# Revit family: Sink-Vessel-Lavatory-KOHLER-Spacity-K-28907T
name_source: partatom
category: Plumbing Fixtures
units: mm (PartAtom-declared; Revit-internal decimal feet)

## family parameters
Cut with Voids When Loaded = No
Host = Face
OmniClass Number = 23.31.13.00
OmniClass Title = Sinks
Part Type = Normal
Room Calculation Point = No
Round Connector Dimension = Use Diameter
Shared = No

## types (1)
- 0-White
    ADA Compliant = No
    Assembly Code = D2010400
    CW Connection = No
    Cold Water Inlet = Cold Water Inlet
    Date Modified = 19/01/2023
    Default Elevation = 36"
    Description = SQUARE VESSEL WITH DECK
    Drain Included = No
    Finish = Kohler-Vitreous_China-0-White
    HW Connection = No
    Height = 7 3/16"
    Hot Water Inlet = Hot Water Inlet
    Length = 14 15/16"
    Manufacturer = Kohler Co.
    Master Format 2014 = 22 41 16
    Master Format 2014 Name = Residential Lavatories and Sinks
    Material = Vitreous China
    Model = K-28907T-1-0
    Product Name = Spacity
    Type = 1
    URL = http://www.kohler.com.cn
    Vent Connection = No
    Waste Connection = Yes
    Waste Water Outlet = Waste Water Outlet
    WaterSense Certified = No
    Width = 13 3/4"

## geometry (parser evidence)
native form markers: Sweep x6
no freeform markers — native parametric forms only
